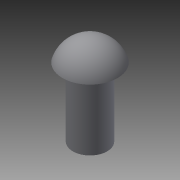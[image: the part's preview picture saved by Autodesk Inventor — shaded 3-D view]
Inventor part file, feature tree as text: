
AUTODESK INVENTOR PART (.ipt)
format: ipt  version: 2015 (Build 190159000, 159)  size: 95,744 bytes
history: native  units: in
note: dims shown in document units (in); Inventor stores cm internally (conversion verified against a paired STEP export)
features: revolve x1, sketch x1
ambient origin geometry x8: Origin, YZ Plane, XZ Plane, XY Plane, X Axis, Y Axis, Z Axis, Center Point
bodies: Solid1 (feature_tree)
feature tree (2):
  revolve  "Revolution1"  [1 undecoded]
  sketch  "Sketch1"  dims[d0=0.5in d1=0.65in d2=0.208in d3=0.075in d4=0.125in d5=90.0deg]
note: 1 required parameter value undecoded (feature->parameter linkage not recoverable at this tier; creation-order binding heuristic only, values carry confidence <= 0.55)
